# Revit family: EZTE-24X16
name_source: partatom
category: Mechanical Equipment
revit_build: Autodesk Revit 2018 (Build: 20170223_1515(x64)
units: mm (PartAtom-declared; Revit-internal decimal feet)

## family parameters
Always vertical = Yes
Cut with Voids When Loaded = No
OmniClass Number = 23.75.00.00
OmniClass Title = Climate Control (HVAC)
Part Type = Normal
Room Calculation Point = No
Round Connector Dimension = Use Diameter
Shared = No
Work Plane-Based = No

## types (2) — shared parameters
Coil = -0' - 8 11/16"
Description = EZTE W/Integral Sound Attenuator
Discharge = 0' - 0 1/32"
DischargeX = 3' - 2"
DischargeY = 1' - 6"
Eheight = 1' - 5 1/2"
ElectricBack = 0' - 1 1/2"
Elength = 2' - 0"
EnclosureCenter = 0' - 9"
EnclosureFront = 0' - 3"
EnclosureHeight = 0' - 11 3/32"
EnclosureWidth = 0' - 7 1/8"
EnslosureRear = 1' - 2 7/32"
Ewidth = 0' - 7 1/8"
Height = 1' - 6"
HeightCenter = 0' - 8 3/4"
InletHeight = 1' - 4"
InletOffset = 0' - 1"
InletWidth = 2' - 0"
Inlet_S = 0' - 5 7/16"
Length = 4' - 5 1/8"
Manufacturer = ANEMOSTAT PRODUCTS
Model = EZTE 24X16
Overlap = 0' - 0 5/8"
SlipDrive = 3' - 8 7/16"
URL = https://www.anemostat-hvac.com
Width = 3' - 2"

## per-type parameters (varying)
| type | LeftController | LeftSide Electric Enclosure | Power Left Controller | Power Right Controller | RightController | RightSide Electric Enclosure |
| EZTE Inlet Size 24x16 LH | Yes | Yes | Yes | No | No | No |
| EZTE Inlet Size 24x16 RH | No | No | No | Yes | Yes | Yes |

## geometry (parser evidence)
native form markers: Sweep x7
no freeform markers — native parametric forms only
